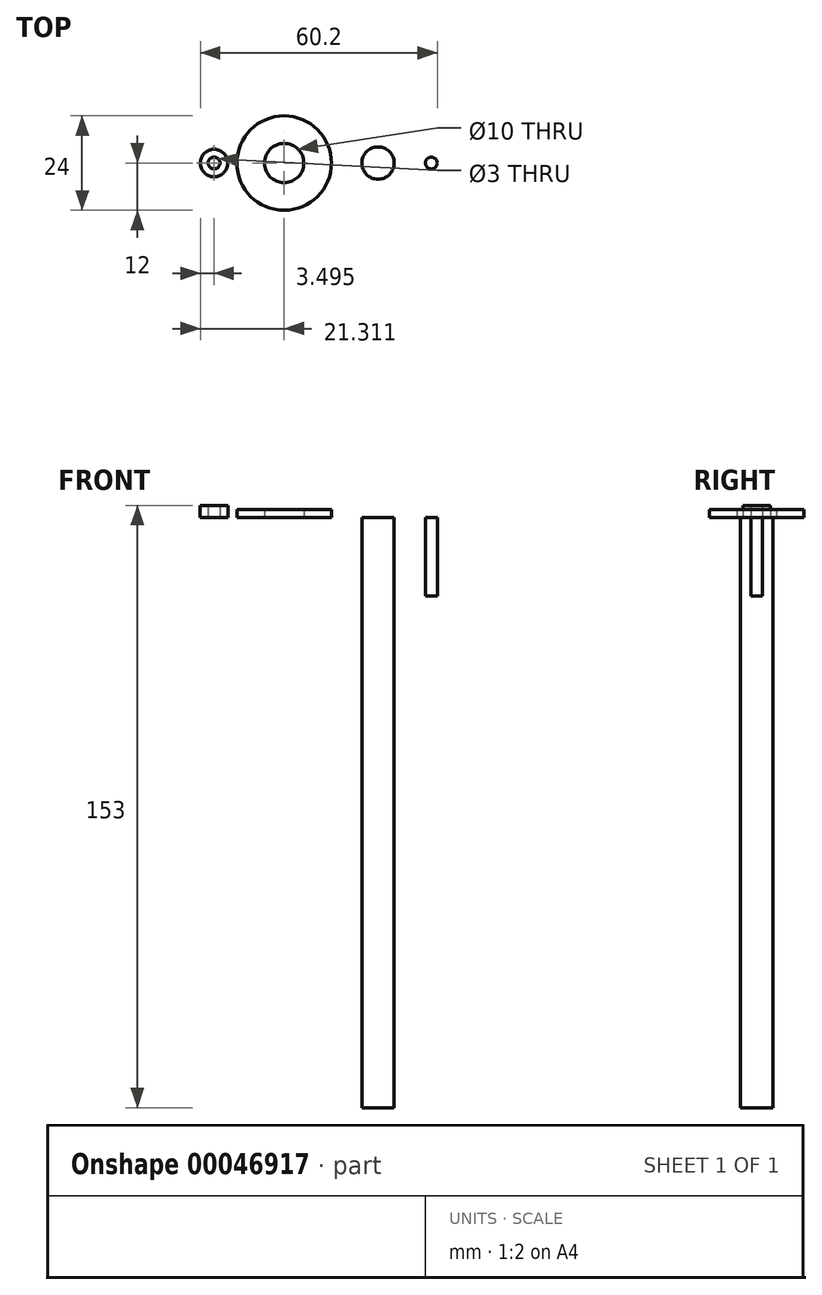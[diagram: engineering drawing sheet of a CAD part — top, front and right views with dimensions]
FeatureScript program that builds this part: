
annotation { "Feature Type Name" : "Feature", "Feature Type Description" : "" }
export const myFeature = defineFeature(function(context is Context, id is Id, definition is map)
    precondition{}
    {
        {
            var Q0;
            Q0=qCreatedBy(makeId("Top.planeOp"),FACE);
            var sketch = newSketch(context, id + "F0", { "sketchPlane" : qUnion([Q0])});
            skCircle(sketch, "E0", {"center": v(-23.57, 0) * mm, "radius": 3.5 * mm});
            skCircle(sketch, "E1", {"center": v(-5.76, 0) * mm, "radius": 12 * mm});
            skCircle(sketch, "E2", {"center": v(-23.57, 0) * mm, "radius": 1.5 * mm});
            skCircle(sketch, "E3", {"center": v(-5.76, 0) * mm, "radius": 5 * mm});
            skCircle(sketch, "E4", {"center": v(18.08, 0) * mm, "radius": 4.1 * mm});
            skCircle(sketch, "E5", {"center": v(31.63, 0) * mm, "radius": 1.5 * mm});
            skSolve(sketch);
        }
        {
            var Q0;
            Q0=makeQuery(id+"F0.imprint","IMPRINT",FACE,{"disambiguationData":[TD([[makeQuery(id+"F0.imprint","IMPRINT",EDGE,{"derivedFrom":sQuery(id+"F0.wireOp",EDGE,"E0")}),1.0]])]});
            extrude(context, id + "F1", {"entities" : qUnion([Q0]), "depth" : 3 * mm});
        }
        {
            var Q0;
            Q0=makeQuery(id+"F0.imprint","IMPRINT",FACE,{"disambiguationData":[TD([[makeQuery(id+"F0.imprint","IMPRINT",EDGE,{"derivedFrom":sQuery(id+"F0.wireOp",EDGE,"E1")}),1.0]])]});
            extrude(context, id + "F2", {"entities" : qUnion([Q0]), "depth" : 2 * mm});
        }
        {
            var Q0;
            Q0=makeQuery(id+"F0.imprint","IMPRINT",FACE,{"disambiguationData":[TD([[makeQuery(id+"F0.imprint","IMPRINT",EDGE,{"derivedFrom":sQuery(id+"F0.wireOp",EDGE,"E4")}),1.0]])]});
            extrude(context, id + "F3", {"entities" : qUnion([Q0]), "oppositeDirection" : true, "depth" : 150 * mm});
        }
        {
            var Q0;
            Q0=makeQuery(id+"F0.imprint","IMPRINT",FACE,{"disambiguationData":[TD([[makeQuery(id+"F0.imprint","IMPRINT",EDGE,{"derivedFrom":sQuery(id+"F0.wireOp",EDGE,"E5")}),1.0]])]});
            extrude(context, id + "F4", {"entities" : qUnion([Q0]), "oppositeDirection" : true, "depth" : 20 * mm});
        }
    });
